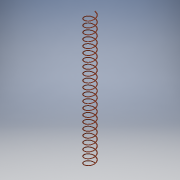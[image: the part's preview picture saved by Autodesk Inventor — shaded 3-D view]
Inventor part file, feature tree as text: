
AUTODESK INVENTOR PART (.ipt)
format: ipt  version: 2018 (Build 220112000, 112)  size: 475,648 bytes
history: native  units: mm
features: helix x1, sketch x1
ambient origin geometry x8: Origin, YZ Plane, XZ Plane, XY Plane, X Axis, Y Axis, Z Axis, Center Point
bodies: Solid1 (feature_tree)
feature tree (2):
  helix  "Coil1"  [1 undecoded]
  sketch  "Sketch1"  dims[d1=4.826mm d2=84.8mm d3=54.3mm d4=54.3mm d5=10.0mm d6=220.0mm d7=0.0mm d8=90.0deg d9=90.0deg d10=0.0mm d11=0.0mm]
note: 1 required parameter value undecoded (feature->parameter linkage not recoverable at this tier; creation-order binding heuristic only, values carry confidence <= 0.55)
